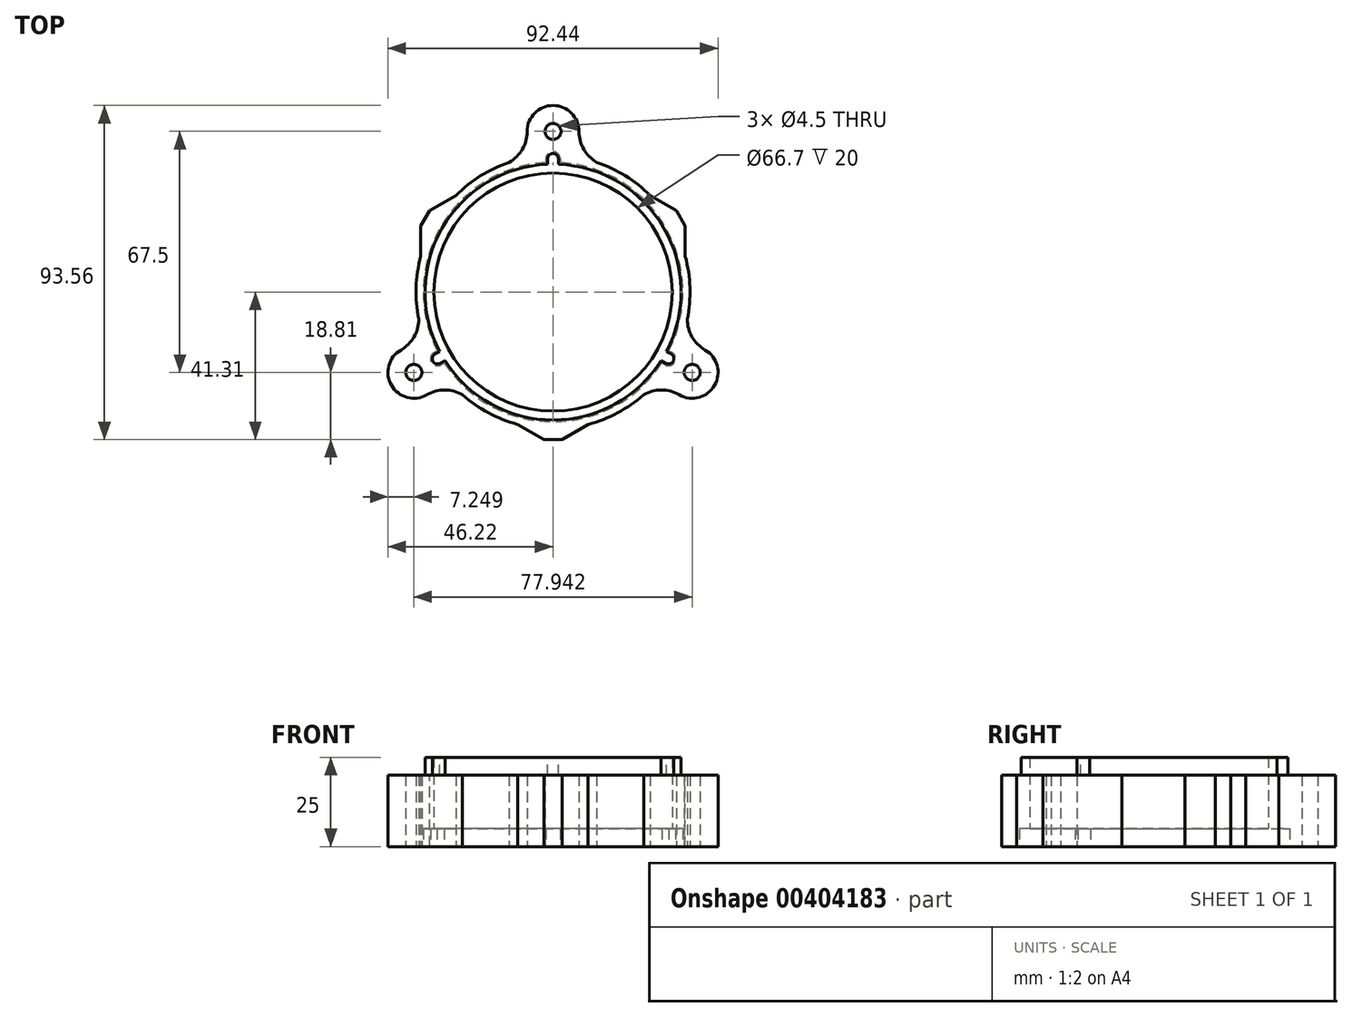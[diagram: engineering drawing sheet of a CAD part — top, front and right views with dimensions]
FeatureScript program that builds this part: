
annotation { "Feature Type Name" : "Feature", "Feature Type Description" : "" }
export const myFeature = defineFeature(function(context is Context, id is Id, definition is map)
    precondition{}
    {
        {
            var Q0;
            Q0=qCreatedBy(makeId("Top.planeOp"),FACE);
            var sketch = newSketch(context, id + "F0", { "sketchPlane" : qUnion([Q0])});
            skCircle(sketch, "E0", {"center": v(0, 0) * mm, "radius": 33.35 * mm});
            skCircle(sketch, "E1", {"center": v(0, 45) * mm, "radius": 2.25 * mm});
            skCircle(sketch, "E2", {"center": v(38.97, -22.5) * mm, "radius": 2.25 * mm});
            skCircle(sketch, "E3", {"center": v(-38.97, -22.5) * mm, "radius": 2.25 * mm});
            skArc(sketch, "E4", {"start": v(-25.35, -28.78) * mm, "mid": v(0, -38.35) * mm, "end": v(25.35, -28.78) * mm});
            skLineSegment(sketch, "E5", {"start": v(0, 0) * mm, "end": v(38.97, -22.5) * mm, "construction": true});
            skLineSegment(sketch, "E6", {"start": v(-38.97, -22.5) * mm, "end": v(0, 0) * mm, "construction": true});
            skArc(sketch, "E7", {"start": v(7.25, 45) * mm, "mid": v(0, 52.25) * mm, "end": v(-7.25, 45) * mm});
            skArc(sketch, "E8.1.0", {"start": v(-42.6, -16.22) * mm, "mid": v(-45.25, -26.12) * mm, "end": v(-35.35, -28.78) * mm});
            skArc(sketch, "E8.2.0", {"start": v(35.35, -28.78) * mm, "mid": v(45.25, -26.12) * mm, "end": v(42.6, -16.22) * mm});
            skArc(sketch, "E9", {"start": v(-12.25, 36.34) * mm, "mid": v(-8.59, 40) * mm, "end": v(-7.25, 45) * mm});
            skArc(sketch, "E10.MirrorCS", {"start": v(12.25, 36.34) * mm, "mid": v(8.59, 40) * mm, "end": v(7.25, 45) * mm});
            skArc(sketch, "E11.1.0", {"start": v(-25.35, -28.78) * mm, "mid": v(-30.35, -27.44) * mm, "end": v(-35.35, -28.78) * mm});
            skArc(sketch, "E11.1.1", {"start": v(-37.6, -7.57) * mm, "mid": v(-38.94, -12.56) * mm, "end": v(-42.6, -16.22) * mm});
            skArc(sketch, "E11.2.0", {"start": v(37.6, -7.57) * mm, "mid": v(38.94, -12.56) * mm, "end": v(42.6, -16.22) * mm});
            skArc(sketch, "E11.2.1", {"start": v(25.35, -28.78) * mm, "mid": v(30.35, -27.44) * mm, "end": v(35.35, -28.78) * mm});
            skArc(sketch, "E12.trimOffspring", {"start": v(37.6, -7.57) * mm, "mid": v(33.21, 19.18) * mm, "end": v(12.25, 36.34) * mm});
            skArc(sketch, "E13.trimOffspring", {"start": v(-12.25, 36.34) * mm, "mid": v(-33.21, 19.17) * mm, "end": v(-37.6, -7.57) * mm});
            skSolve(sketch);
        }
        {
            var Q0;
            Q0 = qSketchRegion(id + "F0", true);
            extrude(context, id + "F1", {"entities" : qUnion([Q0]), "depth" : 20 * mm});
        }
        {
            var Q0;
            Q0=qCreatedBy(makeId("Top.planeOp"),FACE);
            var sketch = newSketch(context, id + "F2", { "sketchPlane" : qUnion([Q0])});
            skCircle(sketch, "E14.cCircle", {"center": v(0, 0) * mm, "radius": 37.02 * mm, "construction": true});
            skLineSegment(sketch, "E14.0", {"start": v(37.02, 21.37) * mm, "end": v(37.02, -21.37) * mm});
            skLineSegment(sketch, "E14.1", {"start": v(37.02, -21.37) * mm, "end": v(0, -42.75) * mm});
            skLineSegment(sketch, "E14.2", {"start": v(0, -42.75) * mm, "end": v(-37.02, -21.37) * mm});
            skLineSegment(sketch, "E14.3", {"start": v(-37.02, -21.37) * mm, "end": v(-37.02, 21.37) * mm});
            skLineSegment(sketch, "E14.4", {"start": v(-37.02, 21.37) * mm, "end": v(0, 42.75) * mm});
            skLineSegment(sketch, "E14.5", {"start": v(0, 42.75) * mm, "end": v(37.02, 21.38) * mm});
            skPoint(sketch, "E14.0.midPoint", {"position": v(37.02, 0) * mm});
            skCircle(sketch, "E15", {"center": v(0, 0) * mm, "radius": 33.35 * mm});
            skSolve(sketch);
        }
        {
            var Q0;
            Q0 = qSketchRegion(id + "F2", true);
            extrude(context, id + "F3", {"entities" : qUnion([Q0]), "operationType" : NewBodyOperationType.ADD, "depth" : 25 * mm});
        }
        {
            var Q0;
            Q0=makeQuery(id+"F3.opExtrude","CAP_FACE",FACE,{"disambiguationData":[OSD([sQuery(id+"F2.wireOp",EDGE,"E14.0"),sQuery(id+"F2.wireOp",EDGE,"E14.1"),sQuery(id+"F2.wireOp",EDGE,"E14.2"),sQuery(id+"F2.wireOp",EDGE,"E14.3"),sQuery(id+"F2.wireOp",EDGE,"E14.4"),sQuery(id+"F2.wireOp",EDGE,"E14.5"),sQuery(id+"F2.wireOp",EDGE,"E15")])],"isStart":false});
            var sketch = newSketch(context, id + "F4", { "sketchPlane" : qUnion([Q0])});
            skArc(sketch, "E16", {"start": v(-1.5, 35.82) * mm, "mid": v(-31.05, 17.93) * mm, "end": v(-31.77, -16.61) * mm});
            skLineSegment(sketch, "E17", {"start": v(0, 38.82) * mm, "end": v(-1.5, 38.82) * mm});
            skLineSegment(sketch, "E18", {"start": v(-1.5, 38.82) * mm, "end": v(-1.5, 35.82) * mm});
            skLineSegment(sketch, "E19.MirrorCS", {"start": v(1.5, 38.82) * mm, "end": v(1.5, 35.82) * mm});
            skLineSegment(sketch, "E20.MirrorCS", {"start": v(0, 38.82) * mm, "end": v(1.5, 38.82) * mm});
            skLineSegment(sketch, "E21.1.0", {"start": v(-34.37, -18.11) * mm, "end": v(-31.77, -16.61) * mm});
            skLineSegment(sketch, "E21.1.1", {"start": v(-32.87, -20.7) * mm, "end": v(-30.27, -19.2) * mm});
            skLineSegment(sketch, "E21.1.2", {"start": v(-33.62, -19.4) * mm, "end": v(-32.87, -20.7) * mm});
            skLineSegment(sketch, "E21.1.3", {"start": v(-33.62, -19.4) * mm, "end": v(-34.37, -18.11) * mm});
            skLineSegment(sketch, "E21.2.0", {"start": v(32.87, -20.7) * mm, "end": v(30.27, -19.2) * mm});
            skLineSegment(sketch, "E21.2.1", {"start": v(34.37, -18.11) * mm, "end": v(31.77, -16.61) * mm});
            skLineSegment(sketch, "E21.2.2", {"start": v(33.62, -19.4) * mm, "end": v(34.37, -18.11) * mm});
            skLineSegment(sketch, "E21.2.3", {"start": v(33.62, -19.4) * mm, "end": v(32.87, -20.7) * mm});
            skArc(sketch, "E22.trimOffspring", {"start": v(31.77, -16.61) * mm, "mid": v(31.05, 17.93) * mm, "end": v(1.5, 35.82) * mm});
            skArc(sketch, "E23.trimOffspring", {"start": v(-30.27, -19.2) * mm, "mid": v(0, -35.85) * mm, "end": v(30.27, -19.2) * mm});
            skCircle(sketch, "E24.cCircle", {"center": v(0, 0) * mm, "radius": 37.02 * mm, "construction": true});
            skLineSegment(sketch, "E24.0", {"start": v(37.02, 21.37) * mm, "end": v(37.02, -21.37) * mm});
            skLineSegment(sketch, "E24.1", {"start": v(37.02, -21.38) * mm, "end": v(0, -42.75) * mm});
            skLineSegment(sketch, "E24.2", {"start": v(0, -42.75) * mm, "end": v(-37.02, -21.38) * mm});
            skLineSegment(sketch, "E24.3", {"start": v(-37.02, -21.38) * mm, "end": v(-37.02, 21.37) * mm});
            skLineSegment(sketch, "E24.4", {"start": v(-37.02, 21.37) * mm, "end": v(0, 42.75) * mm});
            skLineSegment(sketch, "E24.5", {"start": v(0, 42.75) * mm, "end": v(37.02, 21.37) * mm});
            skPoint(sketch, "E24.0.midPoint", {"position": v(37.02, 0) * mm});
            skSolve(sketch);
        }
        {
            var Q0;
            Q0 = qSketchRegion(id + "F4", true);
            extrude(context, id + "F5", {"entities" : qUnion([Q0]), "operationType" : NewBodyOperationType.REMOVE, "oppositeDirection" : true, "depth" : 5 * mm});
        }
        {
            var Q0;
            Q0=makeQuery(id+"F5.boolean.opBoolean","COPY",EDGE,{"derivedFrom":makeQuery(id+"F5.opExtrude","SWEPT_EDGE",EDGE,{"disambiguationData":[OSD([sQuery(id+"F4.wireOp",EDGE,"E21.1.1"),sQuery(id+"F4.wireOp",EDGE,"E21.1.2")])]})});
            var Q1;
            Q1=makeQuery(id+"F5.boolean.opBoolean","COPY",EDGE,{"derivedFrom":makeQuery(id+"F5.opExtrude","SWEPT_EDGE",EDGE,{"disambiguationData":[OSD([sQuery(id+"F4.wireOp",EDGE,"E21.1.0"),sQuery(id+"F4.wireOp",EDGE,"E21.1.3")])]})});
            var Q2;
            Q2=makeQuery(id+"F5.boolean.opBoolean","COPY",EDGE,{"derivedFrom":makeQuery(id+"F5.opExtrude","SWEPT_EDGE",EDGE,{"disambiguationData":[OSD([sQuery(id+"F4.wireOp",EDGE,"E21.2.0"),sQuery(id+"F4.wireOp",EDGE,"E21.2.3")])]})});
            var Q3;
            Q3=makeQuery(id+"F5.boolean.opBoolean","COPY",EDGE,{"derivedFrom":makeQuery(id+"F5.opExtrude","SWEPT_EDGE",EDGE,{"disambiguationData":[OSD([sQuery(id+"F4.wireOp",EDGE,"E21.2.1"),sQuery(id+"F4.wireOp",EDGE,"E21.2.2")])]})});
            var Q4;
            Q4=makeQuery(id+"F5.boolean.opBoolean","COPY",EDGE,{"derivedFrom":makeQuery(id+"F5.opExtrude","SWEPT_EDGE",EDGE,{"disambiguationData":[OSD([sQuery(id+"F4.wireOp",EDGE,"E19.MirrorCS"),sQuery(id+"F4.wireOp",EDGE,"E20.MirrorCS")])]})});
            var Q5;
            Q5=makeQuery(id+"F5.boolean.opBoolean","COPY",EDGE,{"derivedFrom":makeQuery(id+"F5.opExtrude","SWEPT_EDGE",EDGE,{"disambiguationData":[OSD([sQuery(id+"F4.wireOp",EDGE,"E17"),sQuery(id+"F4.wireOp",EDGE,"E18")])]})});
            fillet(context, id + "F6", {"entities" : qUnion([Q0, Q1, Q2, Q3, Q4, Q5]), "radius" : 1.5 * mm, "tangentPropagation" : true, "allowEdgeOverflow" : false});
        }
        {
            var Q0;
            Q0=qCreatedBy(makeId("Top.planeOp"),FACE);
            var sketch = newSketch(context, id + "F7", { "sketchPlane" : qUnion([Q0])});
            skArc(sketch, "E25", {"start": v(-30.43, -19.88) * mm, "mid": v(0, -36.35) * mm, "end": v(30.43, -19.88) * mm});
            skArc(sketch, "E26", {"start": v(2, 37.32) * mm, "mid": v(0, 39.32) * mm, "end": v(-2, 37.32) * mm});
            skLineSegment(sketch, "E27", {"start": v(-2, 37.32) * mm, "end": v(-2, 36.3) * mm});
            skLineSegment(sketch, "E28.MirrorCS", {"start": v(2, 37.32) * mm, "end": v(2, 36.3) * mm});
            skLineSegment(sketch, "E29.1.0", {"start": v(-33.32, -16.93) * mm, "end": v(-32.43, -16.42) * mm});
            skArc(sketch, "E29.1.1", {"start": v(-33.32, -16.93) * mm, "mid": v(-34.05, -19.66) * mm, "end": v(-31.32, -20.4) * mm});
            skLineSegment(sketch, "E29.1.2", {"start": v(-31.32, -20.4) * mm, "end": v(-30.43, -19.88) * mm});
            skLineSegment(sketch, "E29.2.0", {"start": v(31.32, -20.4) * mm, "end": v(30.43, -19.88) * mm});
            skArc(sketch, "E29.2.1", {"start": v(31.32, -20.4) * mm, "mid": v(34.05, -19.66) * mm, "end": v(33.32, -16.93) * mm});
            skLineSegment(sketch, "E29.2.2", {"start": v(33.32, -16.93) * mm, "end": v(32.43, -16.42) * mm});
            skArc(sketch, "E30.trimOffspring", {"start": v(32.43, -16.42) * mm, "mid": v(31.48, 18.18) * mm, "end": v(2, 36.3) * mm});
            skArc(sketch, "E31.trimOffspring", {"start": v(-2, 36.3) * mm, "mid": v(-31.48, 18.17) * mm, "end": v(-32.43, -16.42) * mm});
            skSolve(sketch);
        }
        {
            var Q0;
            Q0 = qSketchRegion(id + "F7", true);
            extrude(context, id + "F8", {"entities" : qUnion([Q0]), "operationType" : NewBodyOperationType.REMOVE, "depth" : 5 * mm});
        }
        {
            var Q0;
            Q0=makeQuery(id+"F3.opExtrude","SWEPT_EDGE",EDGE,{"disambiguationData":[OSD([sQuery(id+"F2.wireOp",EDGE,"E14.1"),sQuery(id+"F2.wireOp",EDGE,"E14.2")])]});
            var Q1;
            Q1=makeQuery(id+"F3.opExtrude","SWEPT_EDGE",EDGE,{"disambiguationData":[OSD([sQuery(id+"F2.wireOp",EDGE,"E14.0"),sQuery(id+"F2.wireOp",EDGE,"E14.5")])]});
            var Q2;
            Q2=makeQuery(id+"F3.opExtrude","SWEPT_EDGE",EDGE,{"disambiguationData":[OSD([sQuery(id+"F2.wireOp",EDGE,"E14.3"),sQuery(id+"F2.wireOp",EDGE,"E14.4")])]});
            chamfer(context, id + "F9", {"entities" : qUnion([Q0, Q1, Q2]), "width" : 5 * mm, "tangentPropagation" : true});
        }
    });
